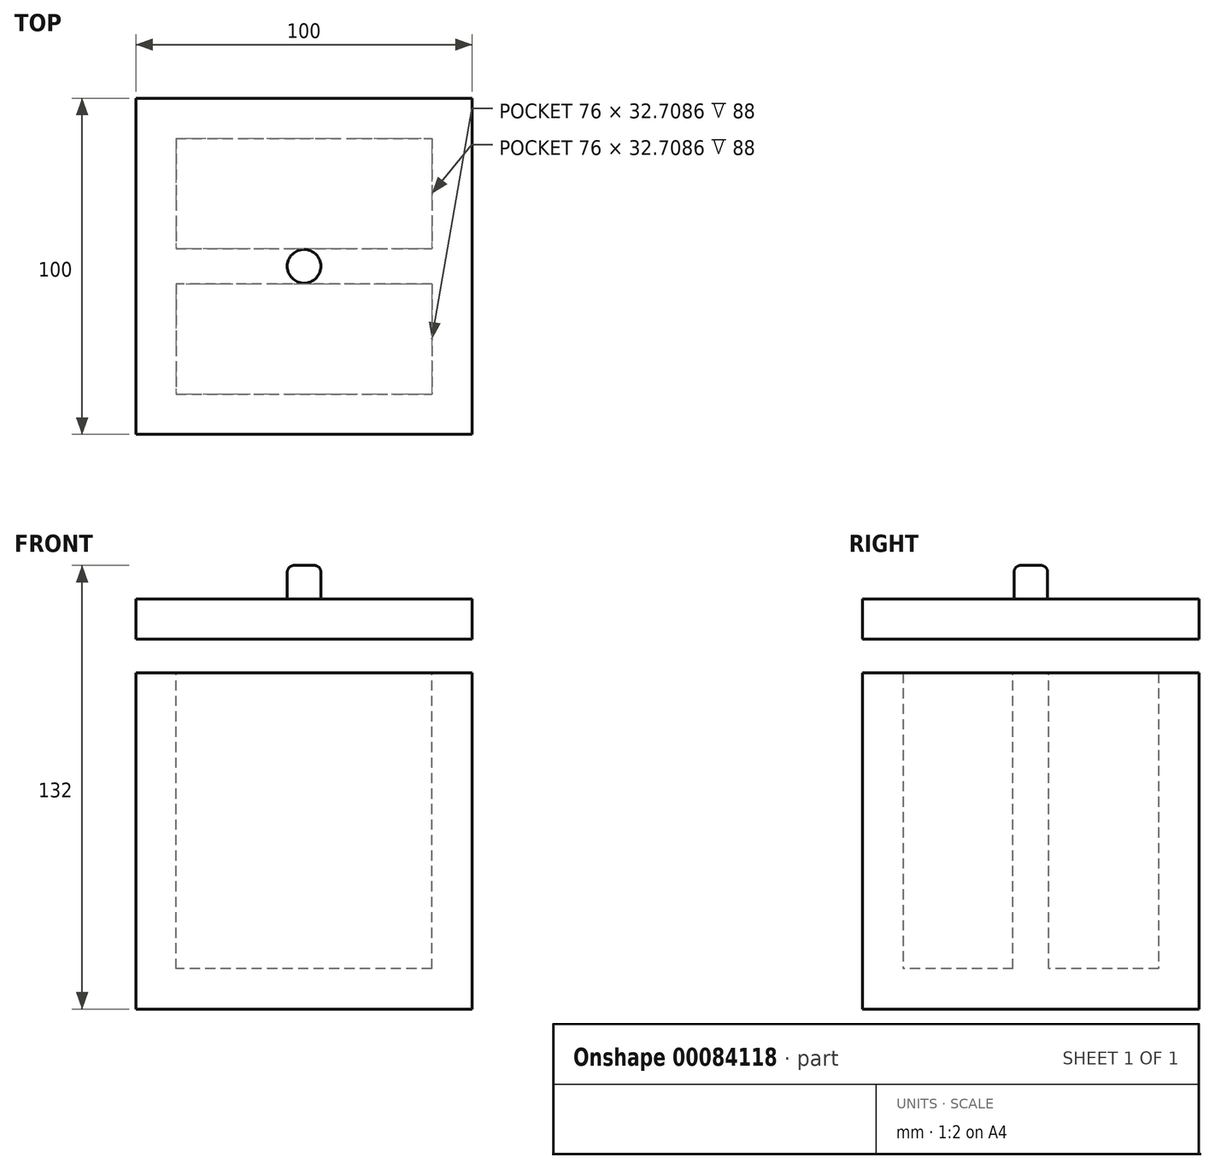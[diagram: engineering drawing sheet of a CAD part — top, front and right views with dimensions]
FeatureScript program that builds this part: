
annotation { "Feature Type Name" : "Feature", "Feature Type Description" : "" }
export const myFeature = defineFeature(function(context is Context, id is Id, definition is map)
    precondition{}
    {
        {
            var Q0;
            Q0=qCreatedBy(makeId("Top.planeOp"),FACE);
            var sketch = newSketch(context, id + "F0", { "sketchPlane" : qUnion([Q0])});
            skLineSegment(sketch, "E0.bottom", {"start": v(-50, 50) * mm, "end": v(50, 50) * mm});
            skLineSegment(sketch, "E0.top", {"start": v(-50, -50) * mm, "end": v(50, -50) * mm});
            skLineSegment(sketch, "E0.left", {"start": v(-50, 50) * mm, "end": v(-50, -50) * mm});
            skLineSegment(sketch, "E0.right", {"start": v(50, 50) * mm, "end": v(50, -50) * mm});
            skPoint(sketch, "E0.middle", {"position": v(0, 0) * mm});
            skSolve(sketch);
        }
        {
            var Q0;
            Q0=makeQuery(id+"F0.imprint","IMPRINT",FACE,{"disambiguationData":[TD([[makeQuery(id+"F0.imprint","IMPRINT",EDGE,{"derivedFrom":sQuery(id+"F0.wireOp",EDGE,"E0.bottom")}),-1.0]])]});
            extrude(context, id + "F1", {"entities" : qUnion([Q0]), "depth" : 100 * mm});
        }
        {
            var Q0;
            Q0=makeQuery(id+"F1.opExtrude","CAP_FACE",FACE,{"disambiguationData":[OSD([sQuery(id+"F0.wireOp",EDGE,"E0.bottom"),sQuery(id+"F0.wireOp",EDGE,"E0.top"),sQuery(id+"F0.wireOp",EDGE,"E0.left"),sQuery(id+"F0.wireOp",EDGE,"E0.right")])],"isStart":false});
            shell(context, id + "F2", {"entities" : qUnion([Q0]), "thickness" : 12 * mm});
        }
        {
            var Q0;
            Q0=qCreatedBy(makeId("Top.planeOp"),FACE);
            var sketch = newSketch(context, id + "F3", { "sketchPlane" : qUnion([Q0])});
            skLineSegment(sketch, "E1.bottom", {"start": v(-50, 5.3) * mm, "end": v(50, 5.3) * mm});
            skLineSegment(sketch, "E1.top", {"start": v(-50, -5.3) * mm, "end": v(50, -5.3) * mm});
            skLineSegment(sketch, "E1.left", {"start": v(-50, 5.3) * mm, "end": v(-50, -5.3) * mm});
            skLineSegment(sketch, "E1.right", {"start": v(50, 5.3) * mm, "end": v(50, -5.3) * mm});
            skPoint(sketch, "E1.middle", {"position": v(0, 0) * mm});
            skSolve(sketch);
        }
        {
            var Q0;
            Q0=makeQuery(id+"F3.imprint","IMPRINT",FACE,{"disambiguationData":[TD([[makeQuery(id+"F3.imprint","IMPRINT",EDGE,{"derivedFrom":sQuery(id+"F3.wireOp",EDGE,"E1.bottom")}),-1.0]])]});
            extrude(context, id + "F4", {"entities" : qUnion([Q0]), "operationType" : NewBodyOperationType.ADD, "depth" : 100 * mm});
        }
        {
            var Q0;
            Q0=makeQuery(id+"F4.boolean.opBoolean","MERGE",FACE,{"derivedFrom":[makeQuery(id+"F1.opExtrude","CAP_FACE",FACE,{"disambiguationData":[OSD([sQuery(id+"F0.wireOp",EDGE,"E0.bottom"),sQuery(id+"F0.wireOp",EDGE,"E0.top"),sQuery(id+"F0.wireOp",EDGE,"E0.left"),sQuery(id+"F0.wireOp",EDGE,"E0.right")])],"isStart":false}),makeQuery(id+"F4.opExtrude","CAP_FACE",FACE,{"disambiguationData":[OSD([sQuery(id+"F3.wireOp",EDGE,"E1.bottom"),sQuery(id+"F3.wireOp",EDGE,"E1.top"),sQuery(id+"F3.wireOp",EDGE,"E1.left"),sQuery(id+"F3.wireOp",EDGE,"E1.right")])],"isStart":false})]});
            cPlane(context, id + "F5", {"entities" : qUnion([Q0]), "cplaneType" : CPlaneType.OFFSET, "offset" : 10 * mm, "width" : 150 * mm, "height" : 150 * mm});
        }
        {
            var Q0;
            Q0=qCreatedBy(id+"F5.planeOp",FACE);
            var sketch = newSketch(context, id + "F6", { "sketchPlane" : qUnion([Q0])});
            skLineSegment(sketch, "E2.bottom", {"start": v(-50, 50) * mm, "end": v(50, 50) * mm});
            skLineSegment(sketch, "E2.top", {"start": v(-50, -50) * mm, "end": v(50, -50) * mm});
            skLineSegment(sketch, "E2.left", {"start": v(-50, 50) * mm, "end": v(-50, -50) * mm});
            skLineSegment(sketch, "E2.right", {"start": v(50, 50) * mm, "end": v(50, -50) * mm});
            skPoint(sketch, "E2.middle", {"position": v(0, 0) * mm});
            skSolve(sketch);
        }
        {
            var Q0;
            Q0=makeQuery(id+"F6.imprint","IMPRINT",FACE,{"disambiguationData":[TD([[makeQuery(id+"F6.imprint","IMPRINT",EDGE,{"derivedFrom":sQuery(id+"F6.wireOp",EDGE,"E2.bottom")}),-1.0]])]});
            extrude(context, id + "F7", {"entities" : qUnion([Q0]), "depth" : 12 * mm});
        }
        {
            var Q0;
            Q0=makeQuery(id+"F7.opExtrude","CAP_FACE",FACE,{"disambiguationData":[OSD([sQuery(id+"F6.wireOp",EDGE,"E2.bottom"),sQuery(id+"F6.wireOp",EDGE,"E2.top"),sQuery(id+"F6.wireOp",EDGE,"E2.left"),sQuery(id+"F6.wireOp",EDGE,"E2.right")])],"isStart":false});
            var sketch = newSketch(context, id + "F8", { "sketchPlane" : qUnion([Q0])});
            skCircle(sketch, "E3", {"center": v(0, 0) * mm, "radius": 5 * mm});
            skSolve(sketch);
        }
        {
            var Q0;
            Q0=makeQuery(id+"F8.imprint","IMPRINT",FACE,{"disambiguationData":[TD([[makeQuery(id+"F8.imprint","IMPRINT",EDGE,{"derivedFrom":sQuery(id+"F8.wireOp",EDGE,"E3")}),1.0]])]});
            extrude(context, id + "F9", {"entities" : qUnion([Q0]), "operationType" : NewBodyOperationType.ADD, "depth" : 10 * mm});
        }
        {
            var Q0;
            Q0=makeQuery(id+"F9.opExtrude","CAP_EDGE",EDGE,{"disambiguationData":[OSD([sQuery(id+"F8.wireOp",EDGE,"E3")])],"isStart":false});
            fillet(context, id + "F10", {"entities" : qUnion([Q0]), "radius" : 2 * mm, "tangentPropagation" : true, "allowEdgeOverflow" : false});
        }
    });
